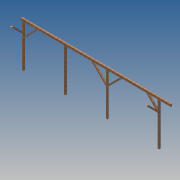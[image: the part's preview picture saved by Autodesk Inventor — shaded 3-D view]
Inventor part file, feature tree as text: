
AUTODESK INVENTOR PART (.ipt)
format: ipt  version: 2013 (Build 170138000, 138)  size: 174,592 bytes
history: native  units: in
note: dims shown in document units (in); Inventor stores cm internally (conversion verified against a paired STEP export)
features: extrude x5, sketch x5
ambient origin geometry x8: Origin, YZ Plane, XZ Plane, XY Plane, X Axis, Y Axis, Z Axis, Center Point
bodies: Solid1 (feature_tree)
feature tree (10):
  extrude  "Extrusion1"  Depth=104.5in
  extrude  "Extrusion2"  Depth=369.0in
  extrude  "Extrusion3"  Depth=3.5in
  extrude  "Extrusion4"  Depth=3.5in
  extrude  "Extrusion5"  Depth=3.5in
  sketch  "Sketch1"  dims[d0=3.5in d1=104.5in]
  sketch  "Sketch2"  dims[d2=30.0in d3=369.0in]
  sketch  "Sketch3"  dims[d4=5.5in d5=3.5in]
  sketch  "Sketch4"  dims[d6=127.25in d7=3.5in]
  sketch  "Sketch5"  dims[d8=103.0in d9=3.5in d10=103.25in d11=135.0deg d12=30.0in d13=3.5in d14=3.5in d15=3.5in d16=0.0in d17=135.0deg d18=3.5in d19=0.0in d20=1.0in d21=1.0in d22=0.0in d23=50.0in d24=135.0deg d25=3.5in d26=3.5in d27=0.0in d28=35.0in d29=45.0deg d30=3.5in d31=3.5in d32=0.0in d33=0.0412in d34=1.1956in d35=35.0in d36=135.0deg]
